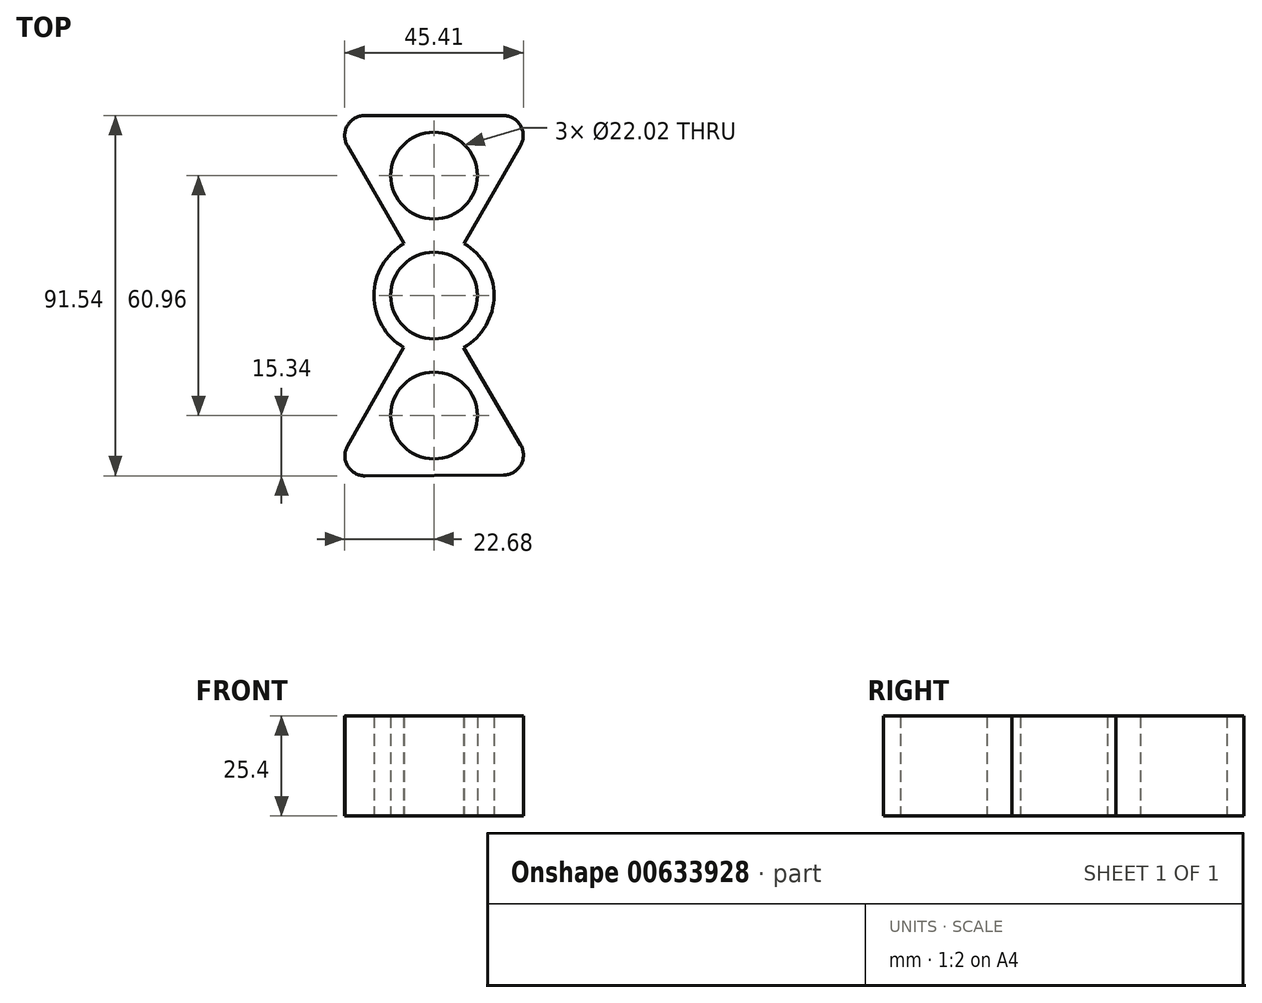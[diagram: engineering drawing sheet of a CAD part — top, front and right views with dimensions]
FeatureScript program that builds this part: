
annotation { "Feature Type Name" : "Feature", "Feature Type Description" : "" }
export const myFeature = defineFeature(function(context is Context, id is Id, definition is map)
    precondition{}
    {
        {
            var Q0;
            Q0=qCreatedBy(makeId("Top.planeOp"),FACE);
            var sketch = newSketch(context, id + "F0", { "sketchPlane" : qUnion([Q0])});
            skCircle(sketch, "E0", {"center": v(0, 0) * mm, "radius": 11.01 * mm});
            skCircle(sketch, "E1", {"center": v(0, 0) * mm, "radius": 15.24 * mm});
            skLineSegment(sketch, "E2", {"start": v(0, 0) * mm, "end": v(0, 30.48) * mm});
            skLineSegment(sketch, "E3", {"start": v(0, 0) * mm, "end": v(0, -30.48) * mm});
            skCircle(sketch, "E4", {"center": v(0, 30.48) * mm, "radius": 11.01 * mm});
            skCircle(sketch, "E5", {"center": v(0, 30.48) * mm, "radius": 15.24 * mm});
            skCircle(sketch, "E6", {"center": v(0, -30.48) * mm, "radius": 15.24 * mm});
            skCircle(sketch, "E7", {"center": v(0, -30.48) * mm, "radius": 11.01 * mm});
            skCircle(sketch, "E8.cCircle", {"center": v(0, 30.48) * mm, "radius": 15.24 * mm, "construction": true});
            skLineSegment(sketch, "E9.0", {"start": v(-26.4, 45.72) * mm, "end": v(26.4, 45.72) * mm});
            skLineSegment(sketch, "E9.1", {"start": v(26.4, 45.72) * mm, "end": v(0, 0) * mm});
            skLineSegment(sketch, "E9.2", {"start": v(0, 0) * mm, "end": v(-26.4, 45.72) * mm});
            skPoint(sketch, "E9.0.midPoint", {"position": v(0, 45.72) * mm});
            skCircle(sketch, "E10.cCircle", {"center": v(0, -30.48) * mm, "radius": 15.24 * mm, "construction": true});
            skLineSegment(sketch, "E10.0", {"start": v(-26.31, -45.86) * mm, "end": v(-0.16, 0) * mm});
            skLineSegment(sketch, "E10.1", {"start": v(-0.16, 0) * mm, "end": v(26.48, -45.58) * mm});
            skLineSegment(sketch, "E10.2", {"start": v(26.48, -45.58) * mm, "end": v(-26.31, -45.86) * mm});
            skPoint(sketch, "E10.0.midPoint", {"position": v(-13.24, -22.93) * mm});
            skSolve(sketch);
        }
        {
            var Q0;
            {var subQ0=sQuery(id+"F0.wireOp",EDGE,"E9.2");var subQ1=sQuery(id+"F0.wireOp",EDGE,"E5");var subQ2=makeQuery(id+"F0.imprint","INTERSECT",VERTEX,{"derivedFrom":[subQ1,subQ0]});Q0=makeQuery(id+"F0.imprint","IMPRINT",FACE,{"disambiguationData":[TD([[makeQuery(id+"F0.imprint","IMPRINT",EDGE,{"disambiguationData":[TD([[subQ2,1.0]])],"derivedFrom":subQ1}),-1.0]])]});}
            var Q1;
            Q1=makeQuery(id+"F0.imprint","IMPRINT",FACE,{"disambiguationData":[TD([[makeQuery(id+"F0.imprint","IMPRINT",EDGE,{"derivedFrom":sQuery(id+"F0.wireOp",EDGE,"E4")}),-1.0]])]});
            var Q2;
            {var subQ0=sQuery(id+"F0.wireOp",EDGE,"E9.0");var subQ1=sQuery(id+"F0.wireOp",EDGE,"E5");var subQ2=makeQuery(id+"F0.imprint","INTERSECT",VERTEX,{"derivedFrom":[subQ1,subQ0]});Q2=makeQuery(id+"F0.imprint","IMPRINT",FACE,{"disambiguationData":[TD([[makeQuery(id+"F0.imprint","IMPRINT",EDGE,{"disambiguationData":[TD([[subQ2,1.0]])],"derivedFrom":subQ1}),-1.0]])]});}
            var Q3;
            {var subQ0=sQuery(id+"F0.wireOp",EDGE,"E9.1");var subQ1=sQuery(id+"F0.wireOp",EDGE,"E1");var subQ2=makeQuery(id+"F0.imprint","INTERSECT",VERTEX,{"derivedFrom":[subQ1,subQ0]});Q3=makeQuery(id+"F0.imprint","IMPRINT",FACE,{"disambiguationData":[TD([[makeQuery(id+"F0.imprint","IMPRINT",EDGE,{"disambiguationData":[TD([[subQ2,1.0]])],"derivedFrom":subQ0}),-1.0]])]});}
            var Q4;
            {var subQ0=sQuery(id+"F0.wireOp",EDGE,"E9.2");var subQ1=sQuery(id+"F0.wireOp",EDGE,"E1");var subQ2=makeQuery(id+"F0.imprint","INTERSECT",VERTEX,{"derivedFrom":[subQ1,subQ0]});Q4=makeQuery(id+"F0.imprint","IMPRINT",FACE,{"disambiguationData":[TD([[makeQuery(id+"F0.imprint","IMPRINT",EDGE,{"disambiguationData":[TD([[subQ2,-1.0]])],"derivedFrom":subQ0}),-1.0]])]});}
            var Q5;
            {var subQ0=sQuery(id+"F0.wireOp",EDGE,"E2");var subQ1=sQuery(id+"F0.wireOp",EDGE,"E0");var subQ2=makeQuery(id+"F0.imprint","INTERSECT",VERTEX,{"derivedFrom":[subQ1,subQ0]});Q5=makeQuery(id+"F0.imprint","IMPRINT",FACE,{"disambiguationData":[TD([[makeQuery(id+"F0.imprint","IMPRINT",EDGE,{"disambiguationData":[TD([[subQ2,-1.0]])],"derivedFrom":subQ1}),-1.0]])]});}
            var Q6;
            {var subQ0=sQuery(id+"F0.wireOp",EDGE,"E2");var subQ1=sQuery(id+"F0.wireOp",EDGE,"E0");var subQ2=makeQuery(id+"F0.imprint","INTERSECT",VERTEX,{"derivedFrom":[subQ1,subQ0]});Q6=makeQuery(id+"F0.imprint","IMPRINT",FACE,{"disambiguationData":[TD([[makeQuery(id+"F0.imprint","IMPRINT",EDGE,{"disambiguationData":[TD([[subQ2,1.0]])],"derivedFrom":subQ1}),-1.0]])]});}
            var Q7;
            {var subQ0=sQuery(id+"F0.wireOp",EDGE,"E9.2");var subQ1=sQuery(id+"F0.wireOp",EDGE,"E0");var subQ2=makeQuery(id+"F0.imprint","INTERSECT",VERTEX,{"derivedFrom":[subQ1,subQ0]});Q7=makeQuery(id+"F0.imprint","IMPRINT",FACE,{"disambiguationData":[TD([[makeQuery(id+"F0.imprint","IMPRINT",EDGE,{"disambiguationData":[TD([[subQ2,-1.0]])],"derivedFrom":subQ1}),-1.0]])]});}
            var Q8;
            {var subQ0=sQuery(id+"F0.wireOp",EDGE,"E10.0");var subQ1=sQuery(id+"F0.wireOp",EDGE,"E0");var subQ2=makeQuery(id+"F0.imprint","INTERSECT",VERTEX,{"derivedFrom":[subQ1,subQ0]});Q8=makeQuery(id+"F0.imprint","IMPRINT",FACE,{"disambiguationData":[TD([[makeQuery(id+"F0.imprint","IMPRINT",EDGE,{"disambiguationData":[TD([[subQ2,-1.0]])],"derivedFrom":subQ1}),-1.0]])]});}
            var Q9;
            {var subQ0=sQuery(id+"F0.wireOp",EDGE,"E3");var subQ1=sQuery(id+"F0.wireOp",EDGE,"E0");var subQ2=makeQuery(id+"F0.imprint","INTERSECT",VERTEX,{"derivedFrom":[subQ1,subQ0]});Q9=makeQuery(id+"F0.imprint","IMPRINT",FACE,{"disambiguationData":[TD([[makeQuery(id+"F0.imprint","IMPRINT",EDGE,{"disambiguationData":[TD([[subQ2,-1.0]])],"derivedFrom":subQ1}),-1.0]])]});}
            var Q10;
            {var subQ0=sQuery(id+"F0.wireOp",EDGE,"E9.1");var subQ1=sQuery(id+"F0.wireOp",EDGE,"E0");var subQ2=makeQuery(id+"F0.imprint","INTERSECT",VERTEX,{"derivedFrom":[subQ1,subQ0]});Q10=makeQuery(id+"F0.imprint","IMPRINT",FACE,{"disambiguationData":[TD([[makeQuery(id+"F0.imprint","IMPRINT",EDGE,{"disambiguationData":[TD([[subQ2,1.0]])],"derivedFrom":subQ1}),-1.0]])]});}
            var Q11;
            Q11=makeQuery(id+"F0.imprint","IMPRINT",FACE,{"disambiguationData":[TD([[makeQuery(id+"F0.imprint","IMPRINT",EDGE,{"derivedFrom":sQuery(id+"F0.wireOp",EDGE,"E7")}),-1.0]])]});
            var Q12;
            {var subQ0=sQuery(id+"F0.wireOp",EDGE,"E10.0");var subQ1=sQuery(id+"F0.wireOp",EDGE,"E1");var subQ2=makeQuery(id+"F0.imprint","INTERSECT",VERTEX,{"derivedFrom":[subQ1,subQ0]});Q12=makeQuery(id+"F0.imprint","IMPRINT",FACE,{"disambiguationData":[TD([[makeQuery(id+"F0.imprint","IMPRINT",EDGE,{"disambiguationData":[TD([[subQ2,1.0]])],"derivedFrom":subQ0}),-1.0]])]});}
            var Q13;
            {var subQ0=sQuery(id+"F0.wireOp",EDGE,"E10.1");var subQ1=sQuery(id+"F0.wireOp",EDGE,"E1");var subQ2=makeQuery(id+"F0.imprint","INTERSECT",VERTEX,{"derivedFrom":[subQ1,subQ0]});Q13=makeQuery(id+"F0.imprint","IMPRINT",FACE,{"disambiguationData":[TD([[makeQuery(id+"F0.imprint","IMPRINT",EDGE,{"disambiguationData":[TD([[subQ2,-1.0]])],"derivedFrom":subQ0}),-1.0]])]});}
            var Q14;
            {var subQ0=sQuery(id+"F0.wireOp",EDGE,"E10.1");var subQ1=sQuery(id+"F0.wireOp",EDGE,"E6");var subQ2=makeQuery(id+"F0.imprint","INTERSECT",VERTEX,{"derivedFrom":[subQ1,subQ0]});Q14=makeQuery(id+"F0.imprint","IMPRINT",FACE,{"disambiguationData":[TD([[makeQuery(id+"F0.imprint","IMPRINT",EDGE,{"disambiguationData":[TD([[subQ2,1.0]])],"derivedFrom":subQ1}),-1.0]])]});}
            var Q15;
            {var subQ0=sQuery(id+"F0.wireOp",EDGE,"E10.0");var subQ1=sQuery(id+"F0.wireOp",EDGE,"E6");var subQ2=makeQuery(id+"F0.imprint","INTERSECT",VERTEX,{"derivedFrom":[subQ1,subQ0]});Q15=makeQuery(id+"F0.imprint","IMPRINT",FACE,{"disambiguationData":[TD([[makeQuery(id+"F0.imprint","IMPRINT",EDGE,{"disambiguationData":[TD([[subQ2,-1.0]])],"derivedFrom":subQ1}),-1.0]])]});}
            extrude(context, id + "F1", {"entities" : qUnion([Q0, Q1, Q2, Q3, Q4, Q5, Q6, Q7, Q8, Q9, Q10, Q11, Q12, Q13, Q14, Q15]), "depth" : 25.4 * mm, "offsetDistance" : 25.4 * mm});
        }
        {
            var Q0;
            Q0=makeQuery(id+"F1.opExtrude","SWEPT_EDGE",EDGE,{"disambiguationData":[OSD([sQuery(id+"F0.wireOp",EDGE,"E9.0"),sQuery(id+"F0.wireOp",EDGE,"E9.1")])]});
            var Q1;
            Q1=makeQuery(id+"F1.opExtrude","SWEPT_EDGE",EDGE,{"disambiguationData":[OSD([sQuery(id+"F0.wireOp",EDGE,"E10.1"),sQuery(id+"F0.wireOp",EDGE,"E10.2")])]});
            var Q2;
            Q2=makeQuery(id+"F1.opExtrude","SWEPT_EDGE",EDGE,{"disambiguationData":[OSD([sQuery(id+"F0.wireOp",EDGE,"E10.0"),sQuery(id+"F0.wireOp",EDGE,"E10.2")])]});
            fillet(context, id + "F2", {"entities" : qUnion([Q0, Q1, Q2]), "radius" : 5.08 * mm, "tangentPropagation" : true, "allowEdgeOverflow" : false});
        }
        {
            var Q0;
            Q0=makeQuery(id+"F1.opExtrude","SWEPT_EDGE",EDGE,{"disambiguationData":[OSD([sQuery(id+"F0.wireOp",EDGE,"E9.0"),sQuery(id+"F0.wireOp",EDGE,"E9.2")])]});
            fillet(context, id + "F3", {"entities" : qUnion([Q0]), "radius" : 5.08 * mm, "tangentPropagation" : true, "allowEdgeOverflow" : false});
        }
    });
